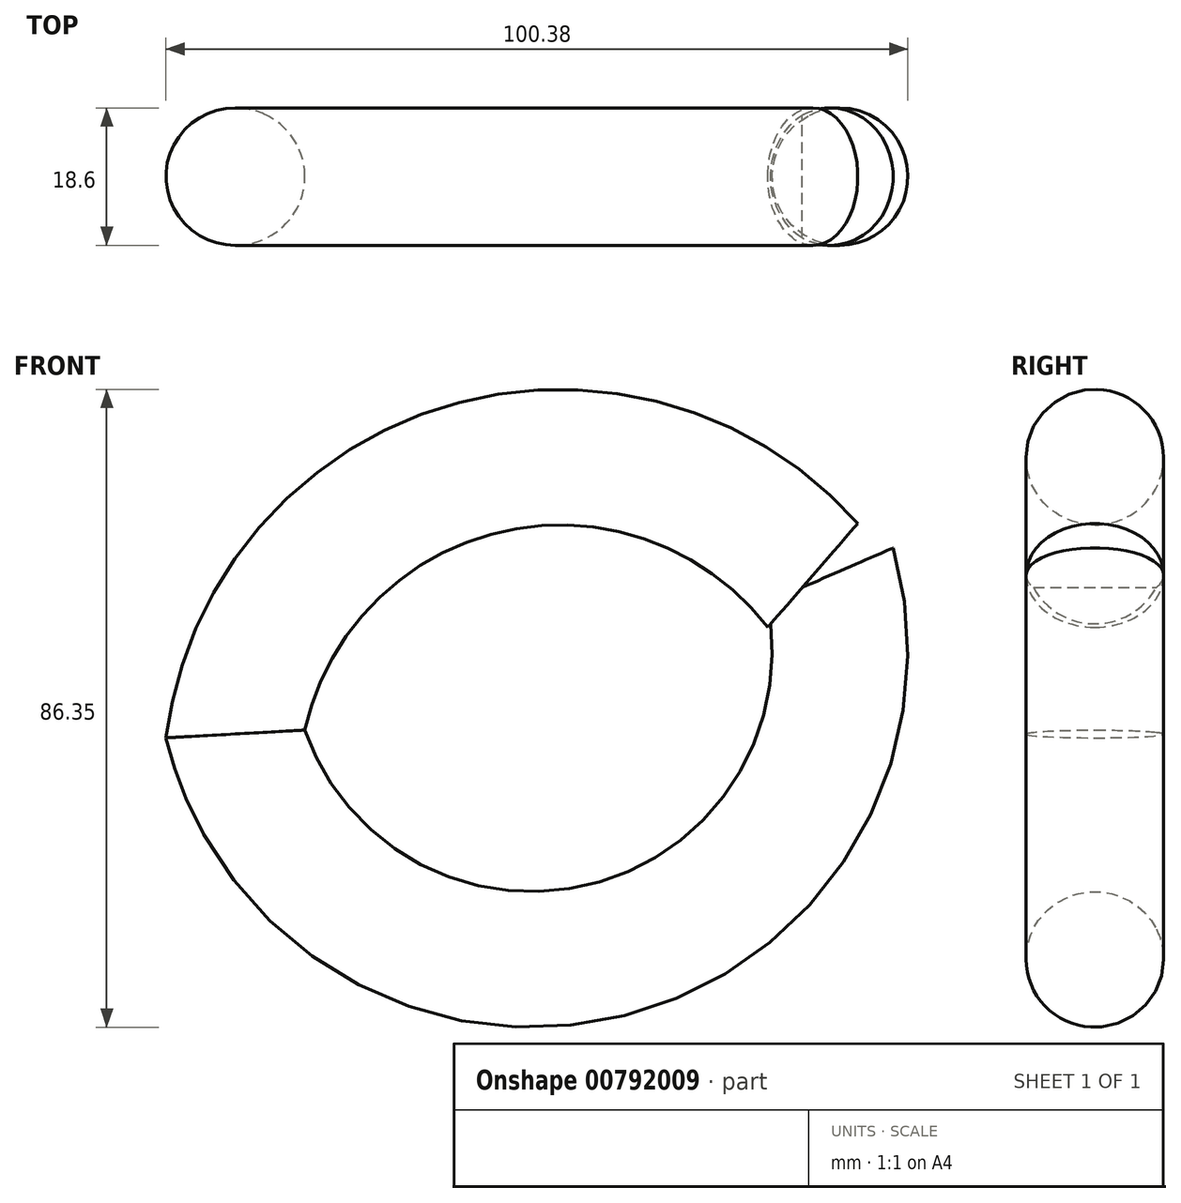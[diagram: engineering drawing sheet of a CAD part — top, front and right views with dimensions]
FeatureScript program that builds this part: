
annotation { "Feature Type Name" : "Feature", "Feature Type Description" : "" }
export const myFeature = defineFeature(function(context is Context, id is Id, definition is map)
    precondition{}
    {
        {
            var Q0;
            Q0=qCreatedBy(makeId("Top.planeOp"),FACE);
            var sketch = newSketch(context, id + "F0", { "sketchPlane" : qUnion([Q0])});
            skCircle(sketch, "E0", {"center": v(0, 0) * mm, "radius": 9.3 * mm});
            skSolve(sketch);
        }
        {
            var Q0;
            Q0=qCreatedBy(makeId("Front.planeOp"),FACE);
            var sketch = newSketch(context, id + "F1", { "sketchPlane" : qUnion([Q0])});
            skArc(sketch, "E1", {"start": v(78.14, 21.48) * mm, "mid": v(32.16, 35.85) * mm, "end": v(0, 0) * mm});
            skArc(sketch, "E2", {"start": v(0, 0) * mm, "mid": v(50.88, -29.1) * mm, "end": v(80.5, 21.48) * mm});
            skArc(sketch, "E3", {"start": v(78.14, 21.48) * mm, "mid": v(79.32, 20.14) * mm, "end": v(80.5, 21.48) * mm});
            skSolve(sketch);
        }
        {
            var Q0;
            Q0=makeQuery(id+"F0.imprint","IMPRINT",FACE,{"disambiguationData":[TD([[makeQuery(id+"F0.imprint","IMPRINT",EDGE,{"derivedFrom":sQuery(id+"F0.wireOp",EDGE,"E0")}),1.0]])]});
            var Q1;
            Q1=sQuery(id+"F1.wireOp",EDGE,"E1");
            var Q2;
            Q2=sQuery(id+"F1.wireOp",EDGE,"E2");
            sweep(context, id + "F2", {"profiles" : qUnion([Q0]), "path" : qUnion([Q1, Q2])});
        }
    });
